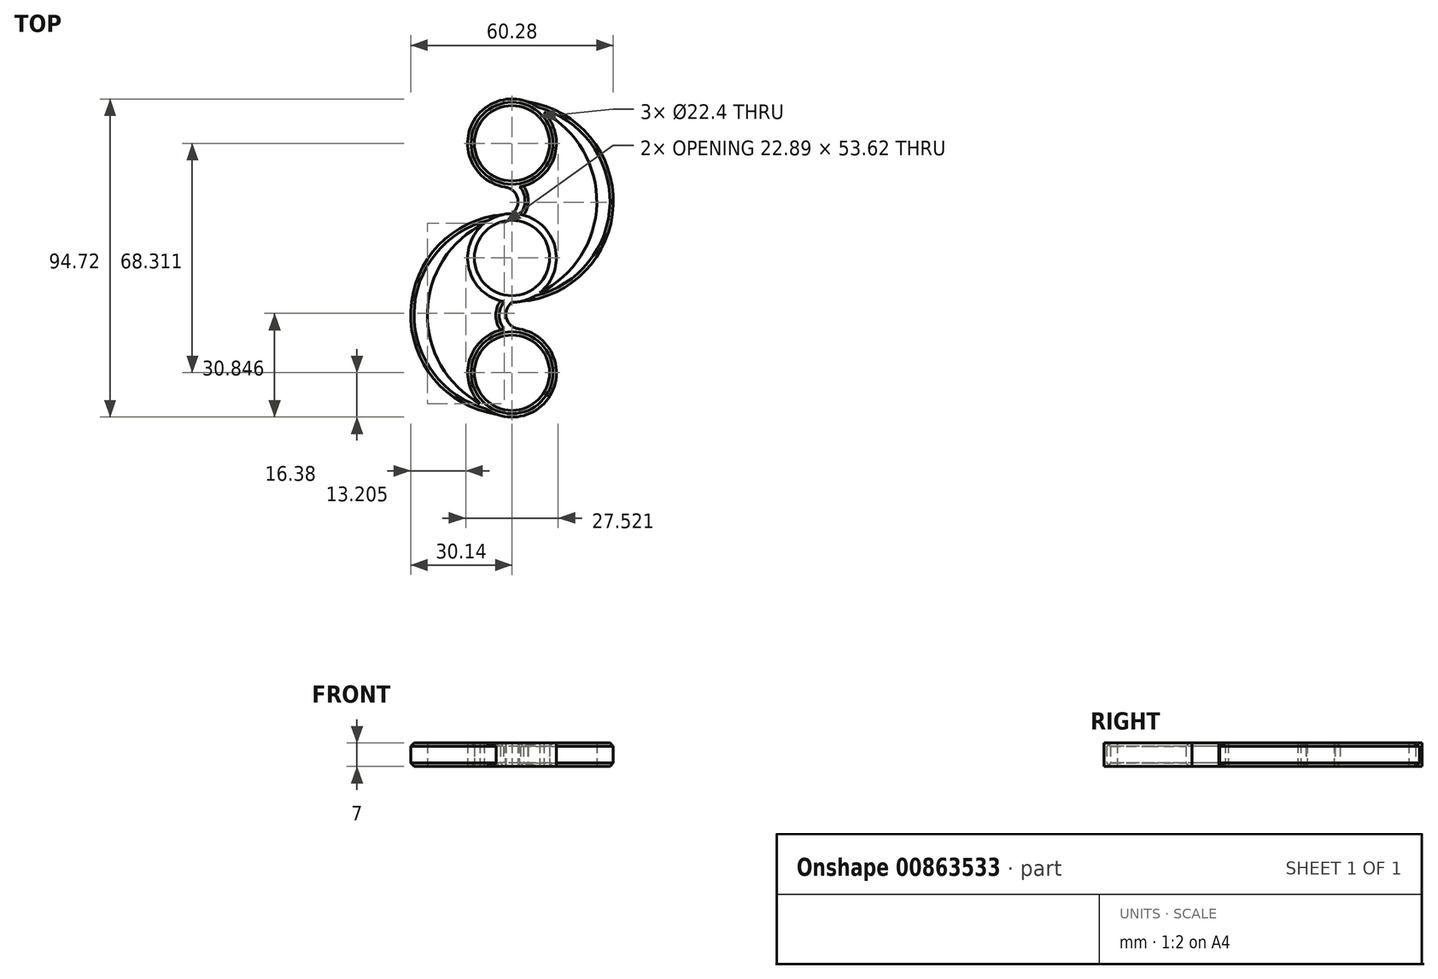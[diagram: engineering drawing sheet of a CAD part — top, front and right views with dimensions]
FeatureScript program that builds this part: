
annotation { "Feature Type Name" : "Feature", "Feature Type Description" : "" }
export const myFeature = defineFeature(function(context is Context, id is Id, definition is map)
    precondition{}
    {
        {
            var Q0;
            Q0=qCreatedBy(makeId("Top.planeOp"),FACE);
            var sketch = newSketch(context, id + "F0", { "sketchPlane" : qUnion([Q0])});
            skCircle(sketch, "E0", {"center": v(0, 0) * mm, "radius": 11.2 * mm});
            skCircle(sketch, "E1", {"center": v(0, 0) * mm, "radius": 13.2 * mm});
            skCircle(sketch, "E2", {"center": v(0, 34.16) * mm, "radius": 11.2 * mm});
            skCircle(sketch, "E3", {"center": v(0, 34.16) * mm, "radius": 13.2 * mm});
            skCircle(sketch, "E4.1.0", {"center": v(0, -34.16) * mm, "radius": 11.2 * mm});
            skCircle(sketch, "E4.1.1", {"center": v(0, -34.16) * mm, "radius": 13.2 * mm});
            skArc(sketch, "E5", {"start": v(0, 13.2) * mm, "mid": v(1.66, 17.88) * mm, "end": v(-2.1, 21.12) * mm});
            skArc(sketch, "E6.1.0", {"start": v(0, -13.2) * mm, "mid": v(-1.66, -17.88) * mm, "end": v(2.1, -21.12) * mm});
            skArc(sketch, "E7", {"start": v(2.56, -12.95) * mm, "mid": v(30.12, 15.84) * mm, "end": v(4.66, 46.5) * mm});
            skArc(sketch, "E8", {"start": v(8.26, -10.3) * mm, "mid": v(25.2, 16.14) * mm, "end": v(9.5, 43.33) * mm});
            skArc(sketch, "E9.1.0", {"start": v(-8.26, 10.3) * mm, "mid": v(-25.2, -16.14) * mm, "end": v(-9.5, -43.33) * mm});
            skArc(sketch, "E9.1.1", {"start": v(-2.56, 12.95) * mm, "mid": v(-30.12, -15.84) * mm, "end": v(-4.66, -46.5) * mm});
            skPoint(sketch, "E10.end.orphan", {"position": v(0, 20.96) * mm});
            skArc(sketch, "E11", {"start": v(1.66, 11.08) * mm, "mid": v(4.83, 17.08) * mm, "end": v(1.66, 23.08) * mm});
            skPoint(sketch, "E11.startSnap0", {"position": v(1.66, 17.88) * mm});
            skPoint(sketch, "E11.endSnap0", {"position": v(1.66, 17.88) * mm});
            skArc(sketch, "E12.1.0", {"start": v(-1.66, -11.08) * mm, "mid": v(-4.83, -17.08) * mm, "end": v(-1.66, -23.08) * mm});
            skSolve(sketch);
        }
        {
            var Q0;
            Q0=makeQuery(id+"F0.imprint","IMPRINT",FACE,{"disambiguationData":[TD([[makeQuery(id+"F0.imprint","IMPRINT",EDGE,{"derivedFrom":sQuery(id+"F0.wireOp",EDGE,"E2")}),-1.0]])]});
            var Q1;
            {var subQ0=sQuery(id+"F0.wireOp",EDGE,"E5");var subQ1=sQuery(id+"F0.wireOp",EDGE,"E1");var subQ2=makeQuery(id+"F0.imprint","INTERSECT",VERTEX,{"derivedFrom":[subQ1,subQ0]});Q1=makeQuery(id+"F0.imprint","IMPRINT",FACE,{"disambiguationData":[TD([[makeQuery(id+"F0.imprint","IMPRINT",EDGE,{"disambiguationData":[TD([[subQ2,1.0]])],"derivedFrom":subQ1}),-1.0]])]});}
            var Q2;
            {var subQ0=sQuery(id+"F0.wireOp",EDGE,"E7");Q2=makeQuery(id+"F0.imprint","IMPRINT",FACE,{"disambiguationData":[TD([[makeQuery(id+"F0.imprint","IMPRINT",EDGE,{"derivedFrom":subQ0}),1.0]])]});}
            var Q3;
            {var subQ3=sQuery(id+"F0.wireOp",EDGE,"E11");var subQ4=sQuery(id+"F0.wireOp",EDGE,"E0");var subQ5=makeQuery(id+"F0.imprint","INTERSECT",VERTEX,{"derivedFrom":[subQ4,subQ3]});Q3=makeQuery(id+"F0.imprint","IMPRINT",FACE,{"disambiguationData":[TD([[makeQuery(id+"F0.imprint","IMPRINT",EDGE,{"disambiguationData":[TD([[subQ5,1.0]])],"derivedFrom":subQ4}),-1.0]])]});}
            var Q4;
            {var subQ0=sQuery(id+"F0.wireOp",EDGE,"E9.1.0");Q4=makeQuery(id+"F0.imprint","IMPRINT",FACE,{"disambiguationData":[TD([[makeQuery(id+"F0.imprint","IMPRINT",EDGE,{"derivedFrom":subQ0}),-1.0]])]});}
            var Q5;
            {var subQ4=sQuery(id+"F0.wireOp",EDGE,"E11");var subQ6=sQuery(id+"F0.wireOp",EDGE,"E0");var subQ7=makeQuery(id+"F0.imprint","INTERSECT",VERTEX,{"derivedFrom":[subQ6,subQ4]});Q5=makeQuery(id+"F0.imprint","IMPRINT",FACE,{"disambiguationData":[TD([[makeQuery(id+"F0.imprint","IMPRINT",EDGE,{"disambiguationData":[TD([[subQ7,-1.0]])],"derivedFrom":subQ6}),-1.0]])]});}
            var Q6;
            {var subQ0=sQuery(id+"F0.wireOp",EDGE,"E6.1.0");var subQ1=sQuery(id+"F0.wireOp",EDGE,"E1");var subQ2=makeQuery(id+"F0.imprint","INTERSECT",VERTEX,{"derivedFrom":[subQ1,subQ0]});Q6=makeQuery(id+"F0.imprint","IMPRINT",FACE,{"disambiguationData":[TD([[makeQuery(id+"F0.imprint","IMPRINT",EDGE,{"disambiguationData":[TD([[subQ2,1.0]])],"derivedFrom":subQ1}),-1.0]])]});}
            var Q7;
            Q7=makeQuery(id+"F0.imprint","IMPRINT",FACE,{"disambiguationData":[TD([[makeQuery(id+"F0.imprint","IMPRINT",EDGE,{"derivedFrom":sQuery(id+"F0.wireOp",EDGE,"E4.1.0")}),-1.0]])]});
            extrude(context, id + "F1", {"entities" : qUnion([Q0, Q1, Q2, Q3, Q4, Q5, Q6, Q7]), "depth" : 7 * mm, "offsetDistance" : 25 * mm});
        }
        {
            var Q0;
            Q0=makeQuery(id+"F1.opExtrude","CAP_EDGE",EDGE,{"disambiguationData":[OSD([sQuery(id+"F0.wireOp",EDGE,"E9.1.1")])],"isStart":false});
            var Q1;
            Q1=makeQuery(id+"F1.opExtrude","CAP_EDGE",EDGE,{"disambiguationData":[OSD([sQuery(id+"F0.wireOp",EDGE,"E7")])],"isStart":false});
            var Q2;
            Q2=makeQuery(id+"F1.opExtrude","CAP_EDGE",EDGE,{"disambiguationData":[OSD([sQuery(id+"F0.wireOp",EDGE,"E12.1.0")])],"isStart":false});
            var Q3;
            Q3=makeQuery(id+"F1.opExtrude","CAP_EDGE",EDGE,{"disambiguationData":[OSD([sQuery(id+"F0.wireOp",EDGE,"E11")])],"isStart":false});
            var Q4;
            Q4=makeQuery(id+"F1.opExtrude","CAP_EDGE",EDGE,{"disambiguationData":[OSD([sQuery(id+"F0.wireOp",EDGE,"E4.1.0")])],"isStart":false});
            var Q5;
            Q5=makeQuery(id+"F1.opExtrude","CAP_EDGE",EDGE,{"disambiguationData":[OSD([sQuery(id+"F0.wireOp",EDGE,"E2")])],"isStart":false});
            chamfer(context, id + "F2", {"entities" : qUnion([Q0, Q1, Q2, Q3, Q4, Q5]), "width" : 1 * mm, "tangentPropagation" : true});
        }
        {
            var Q0;
            Q0=makeQuery(id+"F1.opExtrude","CAP_EDGE",EDGE,{"disambiguationData":[OSD([sQuery(id+"F0.wireOp",EDGE,"E9.1.1")])],"isStart":true});
            var Q1;
            Q1=makeQuery(id+"F1.opExtrude","CAP_EDGE",EDGE,{"disambiguationData":[OSD([sQuery(id+"F0.wireOp",EDGE,"E7")])],"isStart":true});
            var Q2;
            Q2=makeQuery(id+"F1.opExtrude","CAP_EDGE",EDGE,{"disambiguationData":[OSD([sQuery(id+"F0.wireOp",EDGE,"E11")])],"isStart":true});
            var Q3;
            Q3=makeQuery(id+"F1.opExtrude","CAP_EDGE",EDGE,{"disambiguationData":[OSD([sQuery(id+"F0.wireOp",EDGE,"E12.1.0")])],"isStart":true});
            var Q4;
            Q4=makeQuery(id+"F1.opExtrude","CAP_EDGE",EDGE,{"disambiguationData":[OSD([sQuery(id+"F0.wireOp",EDGE,"E4.1.0")])],"isStart":true});
            var Q5;
            Q5=makeQuery(id+"F1.opExtrude","CAP_EDGE",EDGE,{"disambiguationData":[OSD([sQuery(id+"F0.wireOp",EDGE,"E2")])],"isStart":true});
            chamfer(context, id + "F3", {"entities" : qUnion([Q0, Q1, Q2, Q3, Q4, Q5]), "width" : 1 * mm, "tangentPropagation" : true});
        }
    });
